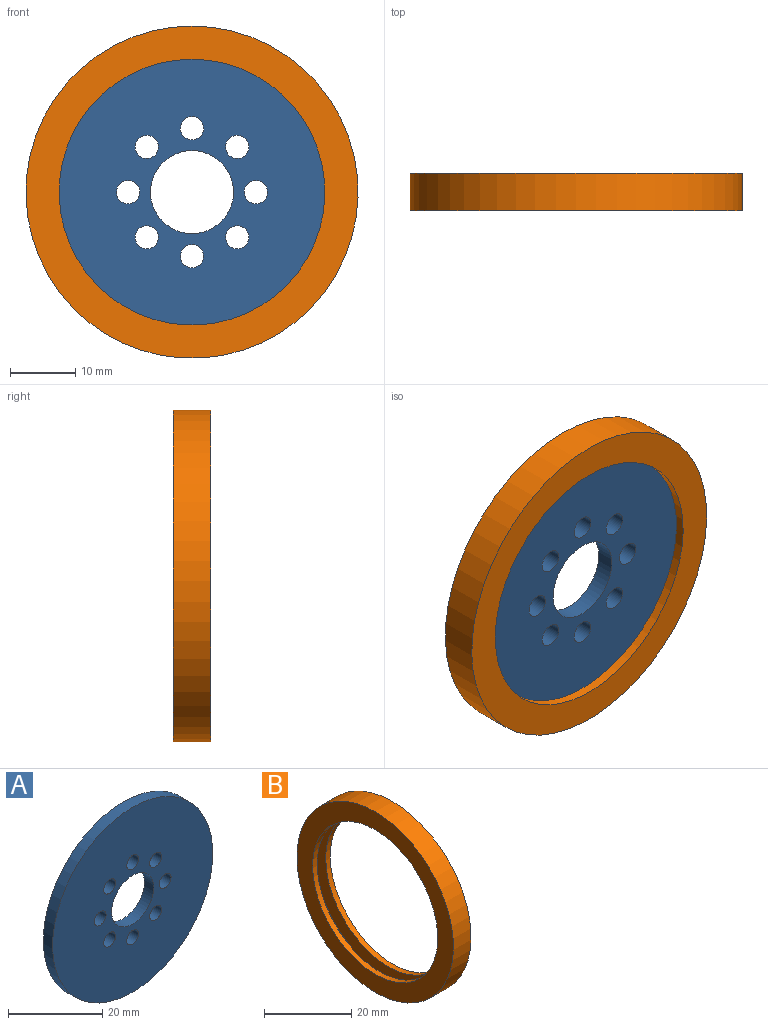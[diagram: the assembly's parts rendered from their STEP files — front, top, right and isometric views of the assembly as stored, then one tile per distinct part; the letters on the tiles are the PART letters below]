
ASSEMBLY  parts=2 mates=1
PART A: 12 faces, bbox 48.2x2.8x48.2 mm
  f0: cylinder r=1.78mm len=3.56mm, axis (0,1,0), area 31.2mm2, adj f10,f11
  f1: cylinder r=1.78mm len=3.56mm, axis (0,1,0), area 31.2mm2, adj f10,f11
  f2: cylinder r=1.78mm len=3.56mm, axis (0,1,0), area 31.2mm2, adj f10,f11
  f3: cylinder r=1.78mm len=3.56mm, axis (0,1,0), area 31.2mm2, adj f10,f11
  f4: cylinder r=1.78mm len=3.56mm, axis (0,1,0), area 31.2mm2, adj f10,f11
  f5: cylinder r=1.78mm len=3.56mm, axis (0,1,0), area 31.2mm2, adj f10,f11
  f6: cylinder r=1.78mm len=3.56mm, axis (0,1,0), area 31.2mm2, adj f10,f11
  f7: cylinder r=1.78mm len=3.56mm, axis (0,1,0), area 31.2mm2, adj f10,f11
  f8: cylinder r=6.35mm len=12.7mm, axis (0,1,0), area 111.5mm2, adj f10,f11
  f9: cylinder r=24.09mm len=48.18mm, axis (0,-1,0), area 422.9mm2, adj f10,f11
  f10: plane 48.18x48.18mm, normal (0,1,0), area 1617.3mm2, adj f0,f1,f2,f3,f4,f5,f6,f7
  f11: plane 48.18x48.18mm, normal (0,-1,0), area 1617.3mm2, adj f0,f1,f2,f3,f4,f5,f6,f7
PART B: 8 faces, bbox 5.7x50.8x50.8 mm
  f0: cylinder r=20.32mm len=40.64mm, axis (-1,0,0), area 186.5mm2, adj f4,f7
  f1: cylinder r=25.4mm len=50.8mm, axis (-1,0,0), area 912.1mm2, adj f6,f7
  f2: cylinder r=20.32mm len=40.64mm, axis (-1,0,0), area 186.5mm2, adj f5,f6
  f3: cylinder r=24.09mm len=48.18mm, axis (-1,0,0), area 422.9mm2, adj f4,f5
  f4: plane 48.18x48.18mm, normal (1,0,0), area 526.3mm2, adj f0,f3
  f5: plane 48.18x48.18mm, normal (-1,0,0), area 526.3mm2, adj f2,f3
  f6: plane 50.8x50.8mm, normal (1,0,0), area 729.7mm2, adj f1,f2
  f7: plane 50.8x50.8mm, normal (-1,0,0), area 729.7mm2, adj f0,f1
PLACE A t=(-52.3,23.68,18.98)mm
PLACE B rot(axis=(0,0,-1),90deg) t=(-52.3,25.07,18.98)mm
MATE fastened B.f0 <-> A.f8  axis (0,1,0) through (-52.3,25.07,18.98)mm
